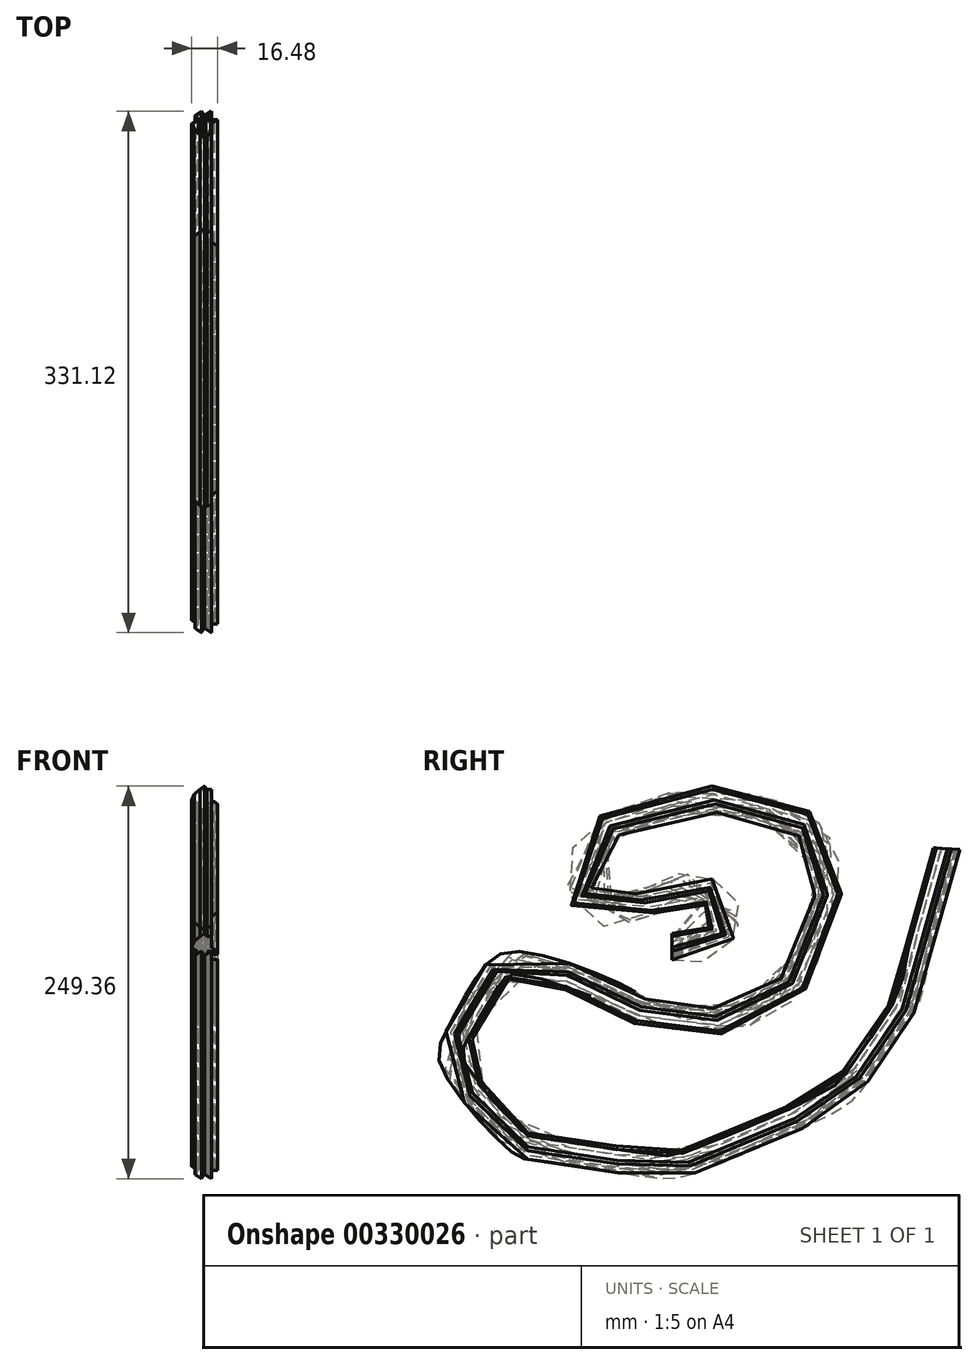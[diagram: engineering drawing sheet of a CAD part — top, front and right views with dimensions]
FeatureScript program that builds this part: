
annotation { "Feature Type Name" : "Feature", "Feature Type Description" : "" }
export const myFeature = defineFeature(function(context is Context, id is Id, definition is map)
    precondition{}
    {
        {
            var Q0;
            Q0=qCreatedBy(makeId("Front.planeOp"),FACE);
            var sketch = newSketch(context, id + "F0", { "sketchPlane" : qUnion([Q0])});
            skLineSegment(sketch, "E0", {"start": v(-6.53, 3.79) * mm, "end": v(-2.87, 6.92) * mm});
            skLineSegment(sketch, "E1", {"start": v(-2.87, 6.92) * mm, "end": v(0, 9) * mm});
            skLineSegment(sketch, "E2", {"start": v(0, 9) * mm, "end": v(1.52, 6.92) * mm});
            skLineSegment(sketch, "E3", {"start": v(1.52, 6.92) * mm, "end": v(4.44, 6.92) * mm});
            skLineSegment(sketch, "E4", {"start": v(4.44, 6.92) * mm, "end": v(4.44, 0) * mm});
            skLineSegment(sketch, "E5", {"start": v(4.44, 0) * mm, "end": v(8.35, -2.48) * mm});
            skLineSegment(sketch, "E6", {"start": v(8.35, -2.48) * mm, "end": v(1.52, -2.48) * mm});
            skLineSegment(sketch, "E7", {"start": v(1.52, -2.48) * mm, "end": v(4.44, -7.96) * mm});
            skLineSegment(sketch, "E8", {"start": v(4.44, -7.96) * mm, "end": v(0, -5.1) * mm});
            skLineSegment(sketch, "E9", {"start": v(0, -5.1) * mm, "end": v(-1.86, -7.96) * mm});
            skLineSegment(sketch, "E10", {"start": v(-1.86, -7.96) * mm, "end": v(-6.08, -5.23) * mm});
            skLineSegment(sketch, "E11", {"start": v(-6.08, -5.23) * mm, "end": v(-4.3, -2.48) * mm});
            skLineSegment(sketch, "E12", {"start": v(-4.3, -2.48) * mm, "end": v(-8.13, 0) * mm});
            skLineSegment(sketch, "E13", {"start": v(-8.13, 0) * mm, "end": v(-6.53, 3.79) * mm});
            skSolve(sketch);
        }
        {
            var Q0;
            Q0=qCreatedBy(makeId("Right.planeOp"),FACE);
            var sketch = newSketch(context, id + "F1", { "sketchPlane" : qUnion([Q0])});
            skFitSpline(sketch, "E14", {"points": [v(0, 0) * mm, v(20.85, 0) * mm, v(35.98, 19.35) * mm, v(26.77, 33.82) * mm, v(0, 37.77) * mm, v(-40.98, 20.01) * mm, v(-60.72, 49.61) * mm, v(-10.07, 89.74) * mm, v(70.18, 85.13) * mm, v(98.47, 56.85) * mm, v(84.65, -8.93) * mm, v(47.16, -43.14) * mm, v(-15.33, -42.48) * mm, v(-27.83, -34.59) * mm, v(-96.24, -10.25) * mm, v(-114, -18.14) * mm, v(-136.36, -56.3) * mm, v(-139, -74.05) * mm, v(-97.55, -123.39) * mm, v(-86.37, -127.33) * mm, v(-9.41, -138.52) * mm, v(13.61, -135.23) * mm, v(105.04, -94.44) * mm, v(118.2, -79.97) * mm, v(147.8, -35.9) * mm, v(155.04, -9.59) * mm, v(174.77, 62.77) * mm], "startDerivative": vector(767.48, -169.3) * mm, "endDerivative": vector(471.28, 1595.78) * mm});
            skSolve(sketch);
        }
        {
            var Q0;
            Q0=makeQuery(id+"F0.imprint","IMPRINT",FACE,{"disambiguationData":[TD([[makeQuery(id+"F0.imprint","IMPRINT",EDGE,{"derivedFrom":sQuery(id+"F0.wireOp",EDGE,"E0")}),-1.0]])]});
            var Q1;
            Q1=sQuery(id+"F1.wireOp",EDGE,"E14");
            sweep(context, id + "F2", {"profiles" : qUnion([Q0]), "path" : qUnion([Q1])});
        }
        {
            var Q0;
            Q0=makeQuery(id+"F2.opSweep","CAP_FACE",FACE,{"disambiguationData":[OSD([sQuery(id+"F0.wireOp",EDGE,"E0"),sQuery(id+"F0.wireOp",EDGE,"E1"),sQuery(id+"F0.wireOp",EDGE,"E2"),sQuery(id+"F0.wireOp",EDGE,"E3"),sQuery(id+"F0.wireOp",EDGE,"E4"),sQuery(id+"F0.wireOp",EDGE,"E5"),sQuery(id+"F0.wireOp",EDGE,"E6"),sQuery(id+"F0.wireOp",EDGE,"E7"),sQuery(id+"F0.wireOp",EDGE,"E8"),sQuery(id+"F0.wireOp",EDGE,"E9"),sQuery(id+"F0.wireOp",EDGE,"E10"),sQuery(id+"F0.wireOp",EDGE,"E11"),sQuery(id+"F0.wireOp",EDGE,"E12"),sQuery(id+"F0.wireOp",EDGE,"E13"),sQuery(id+"F1.wireOp",VERTEX,"E14.end")])],"isStart":false});
            shell(context, id + "F3", {"entities" : qUnion([Q0]), "thickness" : 0.5 * mm});
        }
    });
